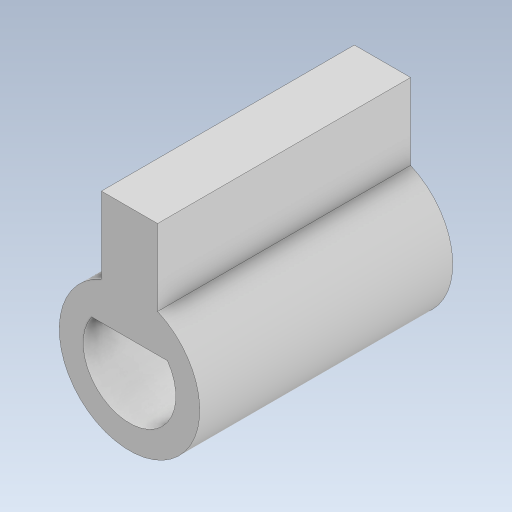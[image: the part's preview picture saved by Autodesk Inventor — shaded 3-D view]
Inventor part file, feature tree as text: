
AUTODESK INVENTOR PART (.ipt)
format: ipt  version: 2023.5 (Build 275446000, 446)  size: 290,816 bytes
history: native  units: in
note: dims shown in document units (in); Inventor stores cm internally (conversion verified against a paired STEP export)
features: extrude x1, sketch x1
ambient origin geometry x8: Origin, YZ Plane, XZ Plane, XY Plane, X Axis, Y Axis, Z Axis, Center Point
bodies: Solid1 (feature_tree)
feature tree (2):
  extrude  "Extrusion1"  Depth=0.0787in
  sketch  "Sketch1"  dims[d5=0.3543in d6=0.0in d16=0.1299in d18=0.0394in d29=0.1969in d30=0.0787in d31=0.1969in d8=0.0197in d9=0.0344in d10=0.0197in d11=0.0344in d20=0.0197in d21=0.0344in d22=0.0197in d23=0.0344in]
